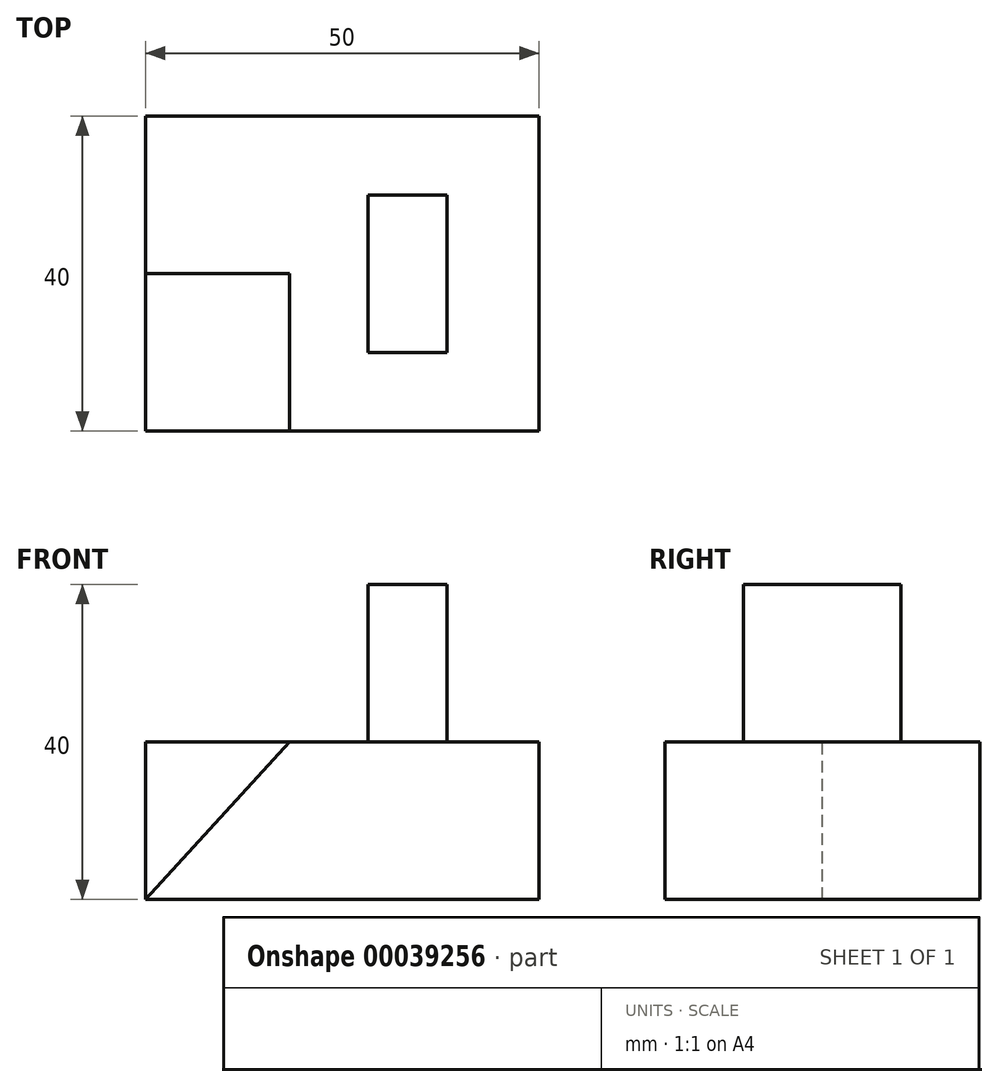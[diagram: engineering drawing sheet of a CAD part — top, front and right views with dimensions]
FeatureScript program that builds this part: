
annotation { "Feature Type Name" : "Feature", "Feature Type Description" : "" }
export const myFeature = defineFeature(function(context is Context, id is Id, definition is map)
    precondition{}
    {
        {
            var Q0;
            Q0=qCreatedBy(makeId("Front.planeOp"),FACE);
            var sketch = newSketch(context, id + "F0", { "sketchPlane" : qUnion([Q0])});
            skLineSegment(sketch, "E0.bottom", {"start": v(1.7, 10.6) * mm, "end": v(31.7, 10.6) * mm});
            skLineSegment(sketch, "E0.top", {"start": v(-18.3, -9.4) * mm, "end": v(31.7, -9.4) * mm});
            skLineSegment(sketch, "E0.right", {"start": v(31.7, 10.6) * mm, "end": v(31.7, -9.4) * mm});
            skPoint(sketch, "E0.left.start.orphan", {"position": v(-18.3, 10.6) * mm});
            skLineSegment(sketch, "E1", {"start": v(-18.3, -9.4) * mm, "end": v(-18.3, 10.6) * mm});
            skLineSegment(sketch, "E2", {"start": v(-18.3, 10.6) * mm, "end": v(1.7, 10.6) * mm});
            skSolve(sketch);
        }
        {
            var Q0;
            Q0=makeQuery(id+"F0.imprint","IMPRINT",FACE,{"disambiguationData":[TD([[makeQuery(id+"F0.imprint","IMPRINT",EDGE,{"derivedFrom":sQuery(id+"F0.wireOp",EDGE,"E0.bottom")}),-1.0]])]});
            extrude(context, id + "F1", {"entities" : qUnion([Q0]), "depth" : 40 * mm});
        }
        {
            var Q0;
            Q0=makeQuery(id+"F1.opExtrude","CAP_FACE",FACE,{"disambiguationData":[OSD([sQuery(id+"F0.wireOp",EDGE,"E0.bottom"),sQuery(id+"F0.wireOp",EDGE,"E0.top"),sQuery(id+"F0.wireOp",EDGE,"E0.right"),sQuery(id+"F0.wireOp",EDGE,"E1"),sQuery(id+"F0.wireOp",EDGE,"E2")])],"isStart":false});
            var sketch = newSketch(context, id + "F2", { "sketchPlane" : qUnion([Q0])});
            skLineSegment(sketch, "E3", {"start": v(-18.3, -9.4) * mm, "end": v(0, 10.6) * mm});
            skSolve(sketch);
        }
        {
            var Q0;
            {var subQ1=sQuery(id+"F2.wireOp",EDGE,"E3");Q0=makeQuery(id+"F2.imprint","IMPRINT",FACE,{"disambiguationData":[TD([[makeQuery(id+"F2.imprint","IMPRINT",EDGE,{"derivedFrom":subQ1}),1.0]])]});}
            extrude(context, id + "F3", {"entities" : qUnion([Q0]), "operationType" : NewBodyOperationType.REMOVE, "oppositeDirection" : true, "depth" : 20 * mm});
        }
        {
            var Q0;
            Q0=makeQuery(id+"F1.opExtrude","SWEPT_FACE",FACE,{"disambiguationData":[OSD([sQuery(id+"F0.wireOp",EDGE,"E0.bottom"),sQuery(id+"F0.wireOp",EDGE,"E2")])]});
            var sketch = newSketch(context, id + "F4", { "sketchPlane" : qUnion([Q0])});
            skLineSegment(sketch, "E4.bottom", {"start": v(10, -10) * mm, "end": v(20, -10) * mm});
            skLineSegment(sketch, "E4.top", {"start": v(10, -30) * mm, "end": v(20, -30) * mm});
            skLineSegment(sketch, "E4.left", {"start": v(10, -10) * mm, "end": v(10, -30) * mm});
            skLineSegment(sketch, "E4.right", {"start": v(20, -10) * mm, "end": v(20, -30) * mm});
            skSolve(sketch);
        }
        {
            var Q0;
            Q0=makeQuery(id+"F4.imprint","IMPRINT",FACE,{"disambiguationData":[TD([[makeQuery(id+"F4.imprint","IMPRINT",EDGE,{"derivedFrom":sQuery(id+"F4.wireOp",EDGE,"E4.bottom")}),-1.0]])]});
            extrude(context, id + "F5", {"entities" : qUnion([Q0]), "operationType" : NewBodyOperationType.ADD, "depth" : 20 * mm});
        }
    });
